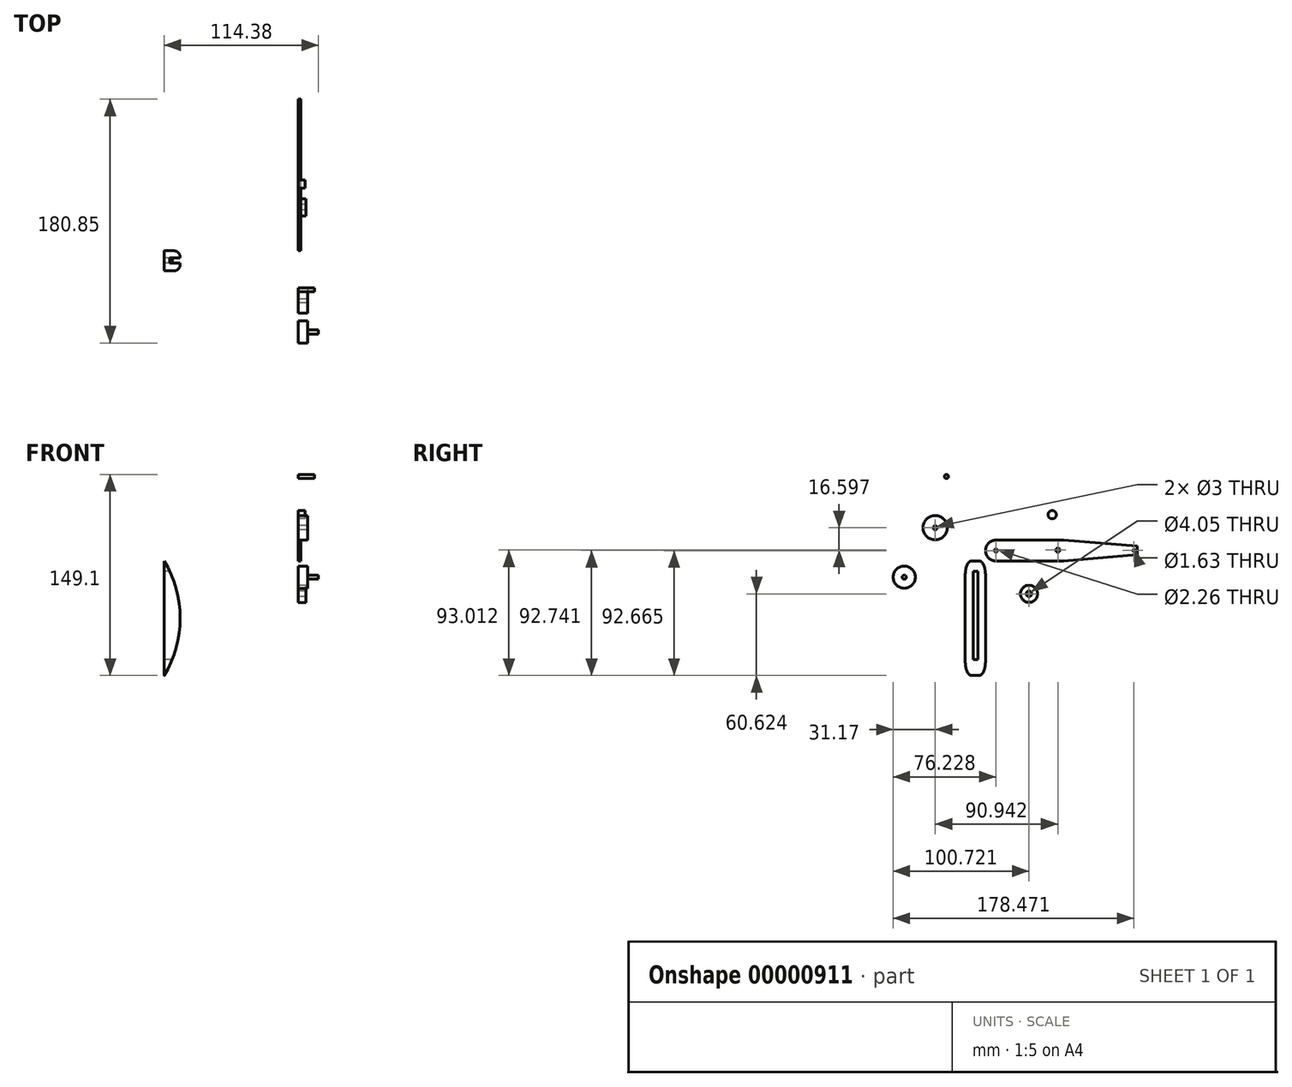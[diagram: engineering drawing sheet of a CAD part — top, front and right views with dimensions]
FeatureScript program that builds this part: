
annotation { "Feature Type Name" : "Feature", "Feature Type Description" : "" }
export const myFeature = defineFeature(function(context is Context, id is Id, definition is map)
    precondition{}
    {
        {
            var Q0;
            Q0=qCreatedBy(makeId("Right.planeOp"),FACE);
            var sketch = newSketch(context, id + "F0", { "sketchPlane" : qUnion([Q0])});
            skLineSegment(sketch, "E0.bottom", {"start": v(6.9, 0) * mm, "end": v(58, 0) * mm});
            skLineSegment(sketch, "E0.top", {"start": v(6.9, 15.33) * mm, "end": v(58, 15.33) * mm});
            skLineSegment(sketch, "E0.right", {"start": v(112.41, 4.58) * mm, "end": v(112.41, 11) * mm});
            skArc(sketch, "E1", {"start": v(6.9, 15.33) * mm, "mid": v(0.07, 7.66) * mm, "end": v(6.9, 0) * mm});
            skPoint(sketch, "E2.orphan", {"position": v(0, 0) * mm});
            skLineSegment(sketch, "E3", {"start": v(58, 15.33) * mm, "end": v(112.41, 11) * mm});
            skLineSegment(sketch, "E4", {"start": v(58, 0) * mm, "end": v(112.41, 4.58) * mm});
            skCircle(sketch, "E5", {"center": v(7.79, 7.66) * mm, "radius": 1.13 * mm});
            skCircle(sketch, "E6", {"center": v(110.03, 7.74) * mm, "radius": 0.81 * mm});
            skCircle(sketch, "E7", {"center": v(53.67, 8.01) * mm, "radius": 1.5 * mm});
            skSolve(sketch);
        }
        {
            var Q0;
            Q0=makeQuery(id+"F0.imprint","IMPRINT",FACE,{"disambiguationData":[TD([[makeQuery(id+"F0.imprint","IMPRINT",EDGE,{"derivedFrom":sQuery(id+"F0.wireOp",EDGE,"E0.bottom")}),1.0]])]});
            extrude(context, id + "F1", {"entities" : qUnion([Q0]), "depth" : 2 * mm});
        }
        {
            var Q0;
            Q0=makeQuery(id+"F1.opExtrude","SWEPT_BODY",BODY,{"disambiguationData":[OSD([sQuery(id+"F0.wireOp",EDGE,"E0.bottom"),sQuery(id+"F0.wireOp",EDGE,"E0.top"),sQuery(id+"F0.wireOp",EDGE,"E0.right"),sQuery(id+"F0.wireOp",EDGE,"E1"),sQuery(id+"F0.wireOp",EDGE,"E3"),sQuery(id+"F0.wireOp",EDGE,"E4"),sQuery(id+"F0.wireOp",EDGE,"E5"),sQuery(id+"F0.wireOp",EDGE,"E6"),sQuery(id+"F0.wireOp",EDGE,"E7")])]});
            var Q1;
            Q1=makeQuery(id+"F1.opExtrude","CAP_EDGE",EDGE,{"disambiguationData":[OSD([sQuery(id+"F0.wireOp",EDGE,"E5")])],"isStart":false});
            transform(context, id + "F2", {"entities" : qUnion([Q0]), "transformType" : TransformType.COPY, "oppositeX" : false, "oppositeY" : false, "oppositeZ" : false});
        }
        {
            var Q0;
            Q0=qCreatedBy(makeId("Right.planeOp"),FACE);
            var sketch = newSketch(context, id + "F3", { "sketchPlane" : qUnion([Q0])});
            skCircle(sketch, "E8", {"center": v(-37.27, 24.6) * mm, "radius": 9 * mm});
            skCircle(sketch, "E9", {"center": v(-37.27, 24.6) * mm, "radius": 1.5 * mm});
            skSolve(sketch);
        }
        {
            var Q0;
            Q0=makeQuery(id+"F3.imprint","IMPRINT",FACE,{"disambiguationData":[TD([[makeQuery(id+"F3.imprint","IMPRINT",EDGE,{"derivedFrom":sQuery(id+"F3.wireOp",EDGE,"E8")}),1.0]])]});
            extrude(context, id + "F4", {"entities" : qUnion([Q0]), "depth" : 7 * mm});
        }
        {
            var Q0;
            Q0=qCreatedBy(makeId("Right.planeOp"),FACE);
            var sketch = newSketch(context, id + "F5", { "sketchPlane" : qUnion([Q0])});
            skCircle(sketch, "E10", {"center": v(49.48, 34.3) * mm, "radius": 3.08 * mm});
            skSolve(sketch);
        }
        {
            var Q0;
            Q0=makeQuery(id+"F5.imprint","IMPRINT",FACE,{"disambiguationData":[TD([[makeQuery(id+"F5.imprint","IMPRINT",EDGE,{"derivedFrom":sQuery(id+"F5.wireOp",EDGE,"E10")}),1.0]])]});
            extrude(context, id + "F6", {"entities" : qUnion([Q0]), "depth" : 5 * mm});
        }
        {
            var Q0;
            Q0=qCreatedBy(makeId("Front.planeOp"),FACE);
            var sketch = newSketch(context, id + "F7", { "sketchPlane" : qUnion([Q0])});
            skLineSegment(sketch, "E11", {"start": v(-99.38, 0) * mm, "end": v(-99.38, -85) * mm});
            skArc(sketch, "E12", {"start": v(-99.38, -85) * mm, "mid": v(-87.5, -42.5) * mm, "end": v(-99.38, 0) * mm});
            skSolve(sketch);
        }
        {
            var Q0;
            Q0=makeQuery(id+"F7.imprint","IMPRINT",FACE,{"disambiguationData":[TD([[makeQuery(id+"F7.imprint","IMPRINT",EDGE,{"derivedFrom":sQuery(id+"F7.wireOp",EDGE,"E11")}),1.0]])]});
            extrude(context, id + "F8", {"entities" : qUnion([Q0]), "depth" : 15 * mm});
        }
        {
            var Q0;
            Q0=makeQuery(id+"F8.opExtrude","CAP_EDGE",EDGE,{"disambiguationData":[OSD([sQuery(id+"F7.wireOp",EDGE,"E12")])],"isStart":false});
            var Q1;
            Q1=makeQuery(id+"F8.opExtrude","CAP_EDGE",EDGE,{"disambiguationData":[OSD([sQuery(id+"F7.wireOp",EDGE,"E12")])],"isStart":true});
            fillet(context, id + "F9", {"entities" : qUnion([Q0, Q1]), "radius" : 5 * mm, "tangentPropagation" : true, "allowEdgeOverflow" : false});
        }
        {
            var Q0;
            Q0=makeQuery(id+"F8.opExtrude","SWEPT_FACE",FACE,{"disambiguationData":[OSD([sQuery(id+"F7.wireOp",EDGE,"E11")])]});
            var sketch = newSketch(context, id + "F10", { "sketchPlane" : qUnion([Q0])});
            skLineSegment(sketch, "E13.bottom", {"start": v(5.45, -7.69) * mm, "end": v(9, -7.69) * mm});
            skLineSegment(sketch, "E13.top", {"start": v(5.45, -73.05) * mm, "end": v(9, -73.05) * mm});
            skLineSegment(sketch, "E13.left", {"start": v(5.45, -7.69) * mm, "end": v(5.45, -73.05) * mm});
            skLineSegment(sketch, "E13.right", {"start": v(9, -7.69) * mm, "end": v(9, -73.05) * mm});
            skSolve(sketch);
        }
        {
            var Q0;
            Q0=makeQuery(id+"F10.imprint","IMPRINT",FACE,{"disambiguationData":[TD([[makeQuery(id+"F10.imprint","IMPRINT",EDGE,{"derivedFrom":sQuery(id+"F10.wireOp",EDGE,"E13.bottom")}),-1.0]])]});
            extrude(context, id + "F11", {"entities" : qUnion([Q0]), "operationType" : NewBodyOperationType.REMOVE, "oppositeDirection" : true, "depth" : 25 * mm});
        }
        {
            var Q0;
            Q0=qCreatedBy(makeId("Right.planeOp"),FACE);
            var sketch = newSketch(context, id + "F12", { "sketchPlane" : qUnion([Q0])});
            skCircle(sketch, "E14", {"center": v(-28.96, 62.6) * mm, "radius": 1.5 * mm});
            skSolve(sketch);
        }
        {
            var Q0;
            Q0=makeQuery(id+"F12.imprint","IMPRINT",FACE,{"disambiguationData":[TD([[makeQuery(id+"F12.imprint","IMPRINT",EDGE,{"derivedFrom":sQuery(id+"F12.wireOp",EDGE,"E14")}),1.0]])]});
            extrude(context, id + "F13", {"entities" : qUnion([Q0]), "depth" : 12 * mm});
        }
        {
            var Q0;
            Q0=qCreatedBy(makeId("Right.planeOp"),FACE);
            var sketch = newSketch(context, id + "F14", { "sketchPlane" : qUnion([Q0])});
            skCircle(sketch, "E15", {"center": v(-60.2, -12.05) * mm, "radius": 8.24 * mm});
            skSolve(sketch);
        }
        {
            var Q0;
            Q0=makeQuery(id+"F14.imprint","IMPRINT",FACE,{"disambiguationData":[TD([[makeQuery(id+"F14.imprint","IMPRINT",EDGE,{"derivedFrom":sQuery(id+"F14.wireOp",EDGE,"E15")}),1.0]])]});
            extrude(context, id + "F15", {"entities" : qUnion([Q0]), "depth" : 15 * mm});
        }
        {
            var Q0;
            Q0=makeQuery(id+"F15.opExtrude","CAP_FACE",FACE,{"disambiguationData":[OSD([sQuery(id+"F14.wireOp",EDGE,"E15")])],"isStart":false});
            var sketch = newSketch(context, id + "F16", { "sketchPlane" : qUnion([Q0])});
            skCircle(sketch, "E16", {"center": v(-60.2, -12.05) * mm, "radius": 1.5 * mm});
            skSolve(sketch);
        }
        {
            var Q0;
            Q0=makeQuery(id+"F16.imprint","IMPRINT",FACE,{"disambiguationData":[TD([[makeQuery(id+"F16.imprint","IMPRINT",EDGE,{"derivedFrom":sQuery(id+"F16.wireOp",EDGE,"E16")}),-1.0]])]});
            extrude(context, id + "F17", {"entities" : qUnion([Q0]), "operationType" : NewBodyOperationType.REMOVE, "oppositeDirection" : true, "depth" : 8 * mm});
        }
        {
            var Q0;
            Q0=qCreatedBy(makeId("Right.planeOp"),FACE);
            var sketch = newSketch(context, id + "F18", { "sketchPlane" : qUnion([Q0])});
            skCircle(sketch, "E17", {"center": v(32.28, -24.38) * mm, "radius": 6.35 * mm});
            skCircle(sketch, "E18", {"center": v(32.28, -24.38) * mm, "radius": 2.02 * mm});
            skSolve(sketch);
        }
        {
            var Q0;
            Q0=makeQuery(id+"F18.imprint","IMPRINT",FACE,{"disambiguationData":[TD([[makeQuery(id+"F18.imprint","IMPRINT",EDGE,{"derivedFrom":sQuery(id+"F18.wireOp",EDGE,"E17")}),1.0]])]});
            extrude(context, id + "F19", {"entities" : qUnion([Q0]), "depth" : 5.56 * mm});
        }
        {
            var Q0;
            Q0=makeQuery(id+"F2.opPattern","COPY",BODY,{"derivedFrom":makeQuery(id+"F1.opExtrude","SWEPT_BODY",BODY,{"disambiguationData":[OSD([sQuery(id+"F0.wireOp",EDGE,"E0.bottom"),sQuery(id+"F0.wireOp",EDGE,"E0.top"),sQuery(id+"F0.wireOp",EDGE,"E0.right"),sQuery(id+"F0.wireOp",EDGE,"E1"),sQuery(id+"F0.wireOp",EDGE,"E3"),sQuery(id+"F0.wireOp",EDGE,"E4"),sQuery(id+"F0.wireOp",EDGE,"E5"),sQuery(id+"F0.wireOp",EDGE,"E6"),sQuery(id+"F0.wireOp",EDGE,"E7")])]}),"instanceName":"1"});
            deleteBodies(context, id + "F20", {"entities" : qUnion([Q0])});
        }
    });
